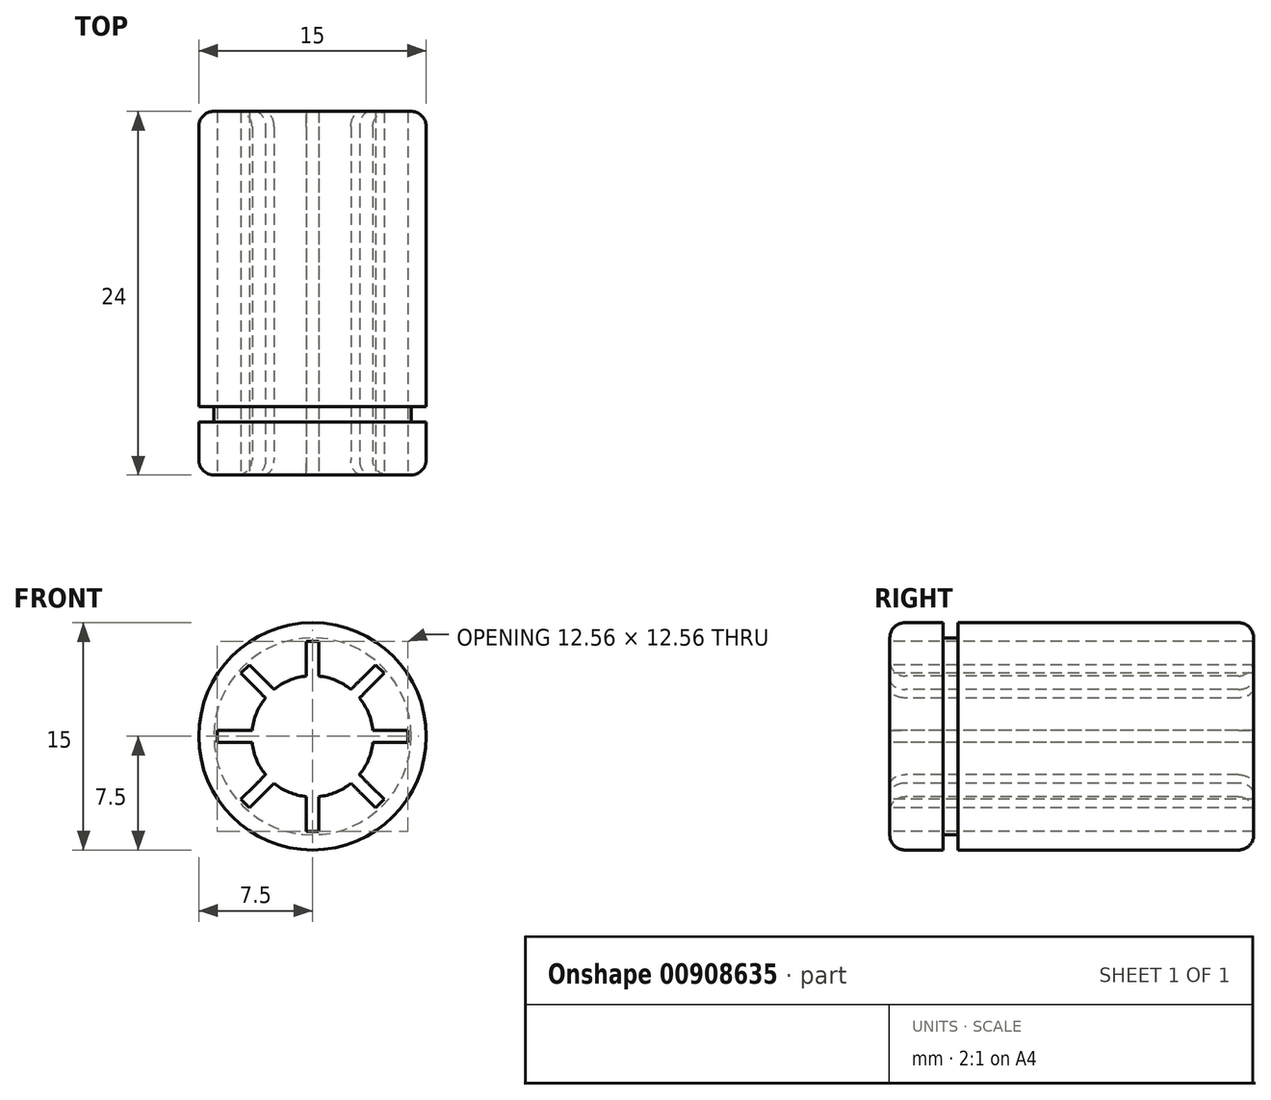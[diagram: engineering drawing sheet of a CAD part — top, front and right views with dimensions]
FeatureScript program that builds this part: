
annotation { "Feature Type Name" : "Feature", "Feature Type Description" : "" }
export const myFeature = defineFeature(function(context is Context, id is Id, definition is map)
    precondition{}
    {
        {
            var Q0;
            Q0=qCreatedBy(makeId("Front.planeOp"),FACE);
            var sketch = newSketch(context, id + "F0", { "sketchPlane" : qUnion([Q0])});
            skCircle(sketch, "E0", {"center": v(0, 0) * mm, "radius": 7.5 * mm});
            skCircle(sketch, "E1", {"center": v(0, 0) * mm, "radius": 4 * mm});
            skLineSegment(sketch, "E2", {"start": v(0, 7.5) * mm, "end": v(0, -7.5) * mm, "construction": true});
            skLineSegment(sketch, "E3", {"start": v(-7.5, 0) * mm, "end": v(7.5, 0) * mm, "construction": true});
            skLineSegment(sketch, "E4", {"start": v(-0.4, 3.98) * mm, "end": v(-0.4, 6.28) * mm});
            skLineSegment(sketch, "E5", {"start": v(-0.4, 6.28) * mm, "end": v(0.4, 6.28) * mm});
            skLineSegment(sketch, "E6", {"start": v(0.4, 6.28) * mm, "end": v(0.4, 3.98) * mm});
            skPoint(sketch, "E7", {"position": v(0, 6.28) * mm});
            skLineSegment(sketch, "E8.1.0", {"start": v(-3.1, 2.53) * mm, "end": v(-4.72, 4.16) * mm});
            skLineSegment(sketch, "E8.1.1", {"start": v(-4.16, 4.72) * mm, "end": v(-2.53, 3.1) * mm});
            skLineSegment(sketch, "E8.1.2", {"start": v(-4.72, 4.16) * mm, "end": v(-4.16, 4.72) * mm});
            skLineSegment(sketch, "E8.2.0", {"start": v(-3.98, -0.4) * mm, "end": v(-6.28, -0.4) * mm});
            skLineSegment(sketch, "E8.2.1", {"start": v(-6.28, 0.4) * mm, "end": v(-3.98, 0.4) * mm});
            skLineSegment(sketch, "E8.2.2", {"start": v(-6.28, -0.4) * mm, "end": v(-6.28, 0.4) * mm});
            skLineSegment(sketch, "E8.3.0", {"start": v(-2.53, -3.1) * mm, "end": v(-4.16, -4.72) * mm});
            skLineSegment(sketch, "E8.3.1", {"start": v(-4.72, -4.16) * mm, "end": v(-3.1, -2.53) * mm});
            skLineSegment(sketch, "E8.3.2", {"start": v(-4.16, -4.72) * mm, "end": v(-4.72, -4.16) * mm});
            skLineSegment(sketch, "E8.4.0", {"start": v(0.4, -3.98) * mm, "end": v(0.4, -6.28) * mm});
            skLineSegment(sketch, "E8.4.1", {"start": v(-0.4, -6.28) * mm, "end": v(-0.4, -3.98) * mm});
            skLineSegment(sketch, "E8.4.2", {"start": v(0.4, -6.28) * mm, "end": v(-0.4, -6.28) * mm});
            skLineSegment(sketch, "E8.5.0", {"start": v(3.1, -2.53) * mm, "end": v(4.72, -4.16) * mm});
            skLineSegment(sketch, "E8.5.1", {"start": v(4.16, -4.72) * mm, "end": v(2.53, -3.1) * mm});
            skLineSegment(sketch, "E8.5.2", {"start": v(4.72, -4.16) * mm, "end": v(4.16, -4.72) * mm});
            skLineSegment(sketch, "E8.6.0", {"start": v(3.98, 0.4) * mm, "end": v(6.28, 0.4) * mm});
            skLineSegment(sketch, "E8.6.1", {"start": v(6.28, -0.4) * mm, "end": v(3.98, -0.4) * mm});
            skLineSegment(sketch, "E8.6.2", {"start": v(6.28, 0.4) * mm, "end": v(6.28, -0.4) * mm});
            skLineSegment(sketch, "E8.7.0", {"start": v(2.53, 3.1) * mm, "end": v(4.16, 4.72) * mm});
            skLineSegment(sketch, "E8.7.1", {"start": v(4.72, 4.16) * mm, "end": v(3.1, 2.53) * mm});
            skLineSegment(sketch, "E8.7.2", {"start": v(4.16, 4.72) * mm, "end": v(4.72, 4.16) * mm});
            skSolve(sketch);
        }
        {
            var Q0;
            Q0 = qSketchRegion(id + "F0", true);
            extrude(context, id + "F1", {"entities" : qUnion([Q0]), "endBound" : BoundingType.SYMMETRIC, "oppositeDirection" : true, "depth" : 24 * mm, "offsetDistance" : 25 * mm});
        }
        {
            var Q0;
            Q0=makeQuery(id+"F1.opExtrude","CAP_EDGE",EDGE,{"disambiguationData":[OSD([sQuery(id+"F0.wireOp",EDGE,"E0")])],"isStart":true});
            var Q1;
            {var subQ0=sQuery(id+"F0.wireOp",EDGE,"E1");Q1=makeQuery(id+"F1.opExtrude","CAP_EDGE",EDGE,{"disambiguationData":[OSD([subQ0]),TDD([makeQuery(id+"F0.imprint","IMPRINT",EDGE,{"disambiguationData":[TD([[makeQuery(id+"F0.imprint","INTERSECT",VERTEX,{"derivedFrom":[subQ0,sQuery(id+"F0.wireOp",EDGE,"E4")]}),-1.0]])],"derivedFrom":subQ0})])],"isStart":true});}
            var Q2;
            {var subQ0=sQuery(id+"F0.wireOp",EDGE,"E1");Q2=makeQuery(id+"F1.opExtrude","CAP_EDGE",EDGE,{"disambiguationData":[OSD([subQ0]),TDD([makeQuery(id+"F0.imprint","IMPRINT",EDGE,{"disambiguationData":[TD([[makeQuery(id+"F0.imprint","INTERSECT",VERTEX,{"derivedFrom":[subQ0,sQuery(id+"F0.wireOp",EDGE,"E8.1.0")]}),-1.0]])],"derivedFrom":subQ0})])],"isStart":true});}
            var Q3;
            {var subQ0=sQuery(id+"F0.wireOp",EDGE,"E1");Q3=makeQuery(id+"F1.opExtrude","CAP_EDGE",EDGE,{"disambiguationData":[OSD([subQ0]),TDD([makeQuery(id+"F0.imprint","IMPRINT",EDGE,{"disambiguationData":[TD([[makeQuery(id+"F0.imprint","INTERSECT",VERTEX,{"derivedFrom":[subQ0,sQuery(id+"F0.wireOp",EDGE,"E8.2.0")]}),-1.0]])],"derivedFrom":subQ0})])],"isStart":true});}
            var Q4;
            {var subQ0=sQuery(id+"F0.wireOp",EDGE,"E1");Q4=makeQuery(id+"F1.opExtrude","CAP_EDGE",EDGE,{"disambiguationData":[OSD([subQ0]),TDD([makeQuery(id+"F0.imprint","IMPRINT",EDGE,{"disambiguationData":[TD([[makeQuery(id+"F0.imprint","INTERSECT",VERTEX,{"derivedFrom":[subQ0,sQuery(id+"F0.wireOp",EDGE,"E8.3.0")]}),-1.0]])],"derivedFrom":subQ0})])],"isStart":true});}
            var Q5;
            {var subQ0=sQuery(id+"F0.wireOp",EDGE,"E1");Q5=makeQuery(id+"F1.opExtrude","CAP_EDGE",EDGE,{"disambiguationData":[OSD([subQ0]),TDD([makeQuery(id+"F0.imprint","IMPRINT",EDGE,{"disambiguationData":[TD([[makeQuery(id+"F0.imprint","INTERSECT",VERTEX,{"derivedFrom":[subQ0,sQuery(id+"F0.wireOp",EDGE,"E8.4.0")]}),-1.0]])],"derivedFrom":subQ0})])],"isStart":true});}
            var Q6;
            {var subQ0=sQuery(id+"F0.wireOp",EDGE,"E1");Q6=makeQuery(id+"F1.opExtrude","CAP_EDGE",EDGE,{"disambiguationData":[OSD([subQ0]),TDD([makeQuery(id+"F0.imprint","IMPRINT",EDGE,{"disambiguationData":[TD([[makeQuery(id+"F0.imprint","INTERSECT",VERTEX,{"derivedFrom":[subQ0,sQuery(id+"F0.wireOp",EDGE,"E8.5.0")]}),-1.0]])],"derivedFrom":subQ0})])],"isStart":true});}
            var Q7;
            {var subQ0=sQuery(id+"F0.wireOp",EDGE,"E1");Q7=makeQuery(id+"F1.opExtrude","CAP_EDGE",EDGE,{"disambiguationData":[OSD([subQ0]),TDD([makeQuery(id+"F0.imprint","IMPRINT",EDGE,{"disambiguationData":[TD([[makeQuery(id+"F0.imprint","INTERSECT",VERTEX,{"derivedFrom":[subQ0,sQuery(id+"F0.wireOp",EDGE,"E8.6.0")]}),-1.0]])],"derivedFrom":subQ0})])],"isStart":true});}
            var Q8;
            {var subQ0=sQuery(id+"F0.wireOp",EDGE,"E1");Q8=makeQuery(id+"F1.opExtrude","CAP_EDGE",EDGE,{"disambiguationData":[OSD([subQ0]),TDD([makeQuery(id+"F0.imprint","IMPRINT",EDGE,{"disambiguationData":[TD([[makeQuery(id+"F0.imprint","INTERSECT",VERTEX,{"derivedFrom":[subQ0,sQuery(id+"F0.wireOp",EDGE,"E6")]}),1.0]])],"derivedFrom":subQ0})])],"isStart":true});}
            var Q9;
            Q9=makeQuery(id+"F1.opExtrude","CAP_EDGE",EDGE,{"disambiguationData":[OSD([sQuery(id+"F0.wireOp",EDGE,"E0")])],"isStart":false});
            var Q10;
            {var subQ0=sQuery(id+"F0.wireOp",EDGE,"E1");Q10=makeQuery(id+"F1.opExtrude","CAP_EDGE",EDGE,{"disambiguationData":[OSD([subQ0]),TDD([makeQuery(id+"F0.imprint","IMPRINT",EDGE,{"disambiguationData":[TD([[makeQuery(id+"F0.imprint","INTERSECT",VERTEX,{"derivedFrom":[subQ0,sQuery(id+"F0.wireOp",EDGE,"E8.5.0")]}),-1.0]])],"derivedFrom":subQ0})])],"isStart":false});}
            var Q11;
            {var subQ0=sQuery(id+"F0.wireOp",EDGE,"E1");Q11=makeQuery(id+"F1.opExtrude","CAP_EDGE",EDGE,{"disambiguationData":[OSD([subQ0]),TDD([makeQuery(id+"F0.imprint","IMPRINT",EDGE,{"disambiguationData":[TD([[makeQuery(id+"F0.imprint","INTERSECT",VERTEX,{"derivedFrom":[subQ0,sQuery(id+"F0.wireOp",EDGE,"E8.6.0")]}),-1.0]])],"derivedFrom":subQ0})])],"isStart":false});}
            var Q12;
            {var subQ0=sQuery(id+"F0.wireOp",EDGE,"E1");Q12=makeQuery(id+"F1.opExtrude","CAP_EDGE",EDGE,{"disambiguationData":[OSD([subQ0]),TDD([makeQuery(id+"F0.imprint","IMPRINT",EDGE,{"disambiguationData":[TD([[makeQuery(id+"F0.imprint","INTERSECT",VERTEX,{"derivedFrom":[subQ0,sQuery(id+"F0.wireOp",EDGE,"E6")]}),1.0]])],"derivedFrom":subQ0})])],"isStart":false});}
            var Q13;
            {var subQ0=sQuery(id+"F0.wireOp",EDGE,"E1");Q13=makeQuery(id+"F1.opExtrude","CAP_EDGE",EDGE,{"disambiguationData":[OSD([subQ0]),TDD([makeQuery(id+"F0.imprint","IMPRINT",EDGE,{"disambiguationData":[TD([[makeQuery(id+"F0.imprint","INTERSECT",VERTEX,{"derivedFrom":[subQ0,sQuery(id+"F0.wireOp",EDGE,"E4")]}),-1.0]])],"derivedFrom":subQ0})])],"isStart":false});}
            var Q14;
            {var subQ0=sQuery(id+"F0.wireOp",EDGE,"E1");Q14=makeQuery(id+"F1.opExtrude","CAP_EDGE",EDGE,{"disambiguationData":[OSD([subQ0]),TDD([makeQuery(id+"F0.imprint","IMPRINT",EDGE,{"disambiguationData":[TD([[makeQuery(id+"F0.imprint","INTERSECT",VERTEX,{"derivedFrom":[subQ0,sQuery(id+"F0.wireOp",EDGE,"E8.1.0")]}),-1.0]])],"derivedFrom":subQ0})])],"isStart":false});}
            var Q15;
            {var subQ0=sQuery(id+"F0.wireOp",EDGE,"E1");Q15=makeQuery(id+"F1.opExtrude","CAP_EDGE",EDGE,{"disambiguationData":[OSD([subQ0]),TDD([makeQuery(id+"F0.imprint","IMPRINT",EDGE,{"disambiguationData":[TD([[makeQuery(id+"F0.imprint","INTERSECT",VERTEX,{"derivedFrom":[subQ0,sQuery(id+"F0.wireOp",EDGE,"E8.2.0")]}),-1.0]])],"derivedFrom":subQ0})])],"isStart":false});}
            var Q16;
            {var subQ0=sQuery(id+"F0.wireOp",EDGE,"E1");Q16=makeQuery(id+"F1.opExtrude","CAP_EDGE",EDGE,{"disambiguationData":[OSD([subQ0]),TDD([makeQuery(id+"F0.imprint","IMPRINT",EDGE,{"disambiguationData":[TD([[makeQuery(id+"F0.imprint","INTERSECT",VERTEX,{"derivedFrom":[subQ0,sQuery(id+"F0.wireOp",EDGE,"E8.3.0")]}),-1.0]])],"derivedFrom":subQ0})])],"isStart":false});}
            var Q17;
            {var subQ0=sQuery(id+"F0.wireOp",EDGE,"E1");Q17=makeQuery(id+"F1.opExtrude","CAP_EDGE",EDGE,{"disambiguationData":[OSD([subQ0]),TDD([makeQuery(id+"F0.imprint","IMPRINT",EDGE,{"disambiguationData":[TD([[makeQuery(id+"F0.imprint","INTERSECT",VERTEX,{"derivedFrom":[subQ0,sQuery(id+"F0.wireOp",EDGE,"E8.4.0")]}),-1.0]])],"derivedFrom":subQ0})])],"isStart":false});}
            fillet(context, id + "F2", {"entities" : qUnion([Q0, Q1, Q2, Q3, Q4, Q5, Q6, Q7, Q8, Q9, Q10, Q11, Q12, Q13, Q14, Q15, Q16, Q17]), "radius" : 1 * mm, "tangentPropagation" : true, "allowEdgeOverflow" : false});
        }
        {
            var Q0;
            Q0=qCreatedBy(makeId("Right.planeOp"),FACE);
            var sketch = newSketch(context, id + "F3", { "sketchPlane" : qUnion([Q0])});
            skLineSegment(sketch, "E9.bottom", {"start": v(-8.5, 7.5) * mm, "end": v(-7.5, 7.5) * mm});
            skLineSegment(sketch, "E9.top", {"start": v(-8.5, 6.5) * mm, "end": v(-7.5, 6.5) * mm});
            skLineSegment(sketch, "E9.left", {"start": v(-8.5, 7.5) * mm, "end": v(-8.5, 6.5) * mm});
            skLineSegment(sketch, "E9.right", {"start": v(-7.5, 7.5) * mm, "end": v(-7.5, 6.5) * mm});
            skLineSegment(sketch, "E10", {"start": v(1, 7.5) * mm, "end": v(23, 7.5) * mm, "construction": true});
            skLineSegment(sketch, "E11", {"start": v(-12.15, 0) * mm, "end": v(34.68, 0) * mm, "construction": true});
            skSolve(sketch);
        }
        {
            var Q0;
            Q0 = qSketchRegion(id + "F3", true);
            var Q1;
            Q1=sQuery(id+"F3.wireOp",EDGE,"E11");
            revolve(context, id + "F4", {"operationType" : NewBodyOperationType.REMOVE, "surfaceOperationType" : NewSurfaceOperationType.NEW, "entities" : qUnion([Q0]), "axis" : qUnion([Q1]), "revolveType" : RevolveType.FULL});
        }
    });
